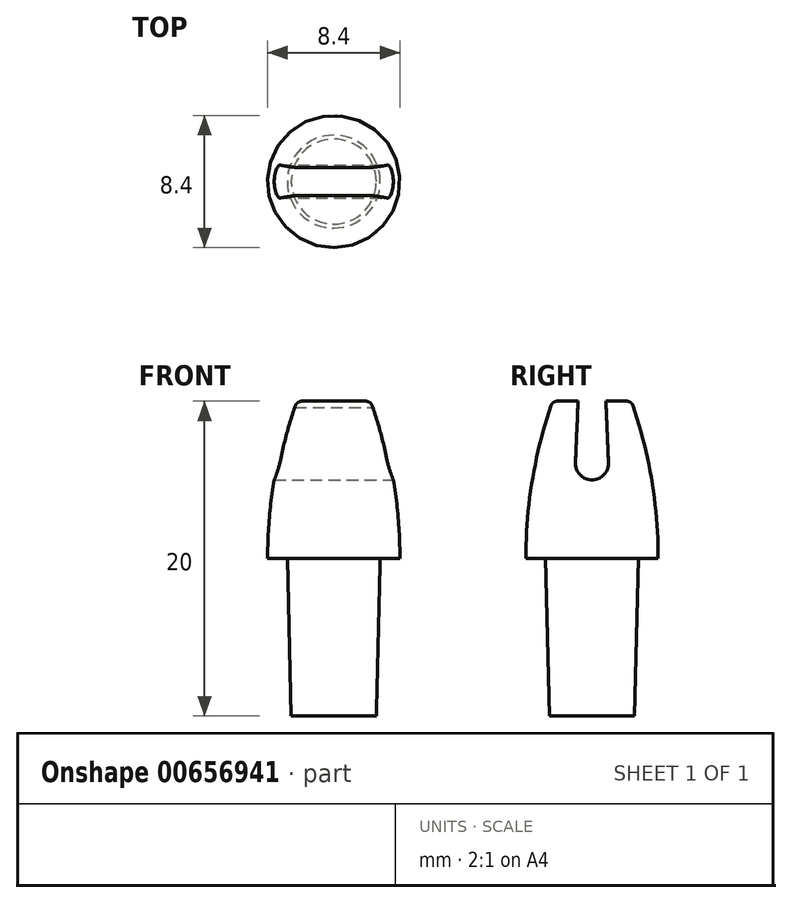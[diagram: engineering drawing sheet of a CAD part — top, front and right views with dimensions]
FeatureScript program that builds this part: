
annotation { "Feature Type Name" : "Feature", "Feature Type Description" : "" }
export const myFeature = defineFeature(function(context is Context, id is Id, definition is map)
    precondition{}
    {
        {
            var Q0;
            Q0=qCreatedBy(makeId("Top.planeOp"),FACE);
            cPlane(context, id + "F0", {"entities" : qUnion([Q0]), "cplaneType" : CPlaneType.OFFSET, "offset" : 10 * mm, "width" : 152.4 * mm, "height" : 152.4 * mm});
        }
        {
            var Q0;
            Q0=qCreatedBy(makeId("Top.planeOp"),FACE);
            var sketch = newSketch(context, id + "F1", { "sketchPlane" : qUnion([Q0])});
            skCircle(sketch, "E0", {"center": v(0, 0) * mm, "radius": 2.7 * mm});
            skSolve(sketch);
        }
        {
            var Q0;
            Q0=qCreatedBy(id+"F0.planeOp",FACE);
            var sketch = newSketch(context, id + "F2", { "sketchPlane" : qUnion([Q0])});
            skCircle(sketch, "E1", {"center": v(0, 0) * mm, "radius": 2.95 * mm});
            skSolve(sketch);
        }
        {
            var Q0;
            Q0=makeQuery(id+"F1.imprint","IMPRINT",FACE,{"disambiguationData":[TD([[makeQuery(id+"F1.imprint","IMPRINT",EDGE,{"derivedFrom":sQuery(id+"F1.wireOp",EDGE,"E0")}),1.0]])]});
            var Q1;
            Q1=makeQuery(id+"F2.imprint","IMPRINT",FACE,{"disambiguationData":[TD([[makeQuery(id+"F2.imprint","IMPRINT",EDGE,{"derivedFrom":sQuery(id+"F2.wireOp",EDGE,"E1")}),1.0]])]});
            loft(context, id + "F3", {"sheetProfilesArray" : [{ "sheetProfileEntities" : qUnion([Q0]) }, { "sheetProfileEntities" : qUnion([Q1]) }]});
        }
        {
            var Q0;
            Q0=qCreatedBy(makeId("Right.planeOp"),FACE);
            var sketch = newSketch(context, id + "F4", { "sketchPlane" : qUnion([Q0])});
            skLineSegment(sketch, "E2", {"start": v(0, 10) * mm, "end": v(-4.2, 10) * mm});
            skArc(sketch, "E3", {"start": v(-4.2, 10) * mm, "mid": v(-3.78, 15.07) * mm, "end": v(-2.5, 20) * mm});
            skLineSegment(sketch, "E4", {"start": v(0, 20) * mm, "end": v(-2.5, 20) * mm});
            skLineSegment(sketch, "E5", {"start": v(0, 10) * mm, "end": v(0, 20) * mm});
            skLineSegment(sketch, "E6", {"start": v(0, 10) * mm, "end": v(0, 0) * mm, "construction": true});
            skSolve(sketch);
        }
        {
            var Q0;
            Q0=makeQuery(id+"F4.imprint","IMPRINT",FACE,{"disambiguationData":[TD([[makeQuery(id+"F4.imprint","IMPRINT",EDGE,{"derivedFrom":sQuery(id+"F4.wireOp",EDGE,"E2")}),-1.0]])]});
            var Q1;
            Q1 = qConstructionFilter(qBodyType(qCreatedBy(id + "F4" ,EDGE), BodyType.WIRE), ConstructionObject.NO);
            var Q2;
            Q2=sQuery(id+"F4.wireOp",EDGE,"E6");
            revolve(context, id + "F5", {"operationType" : NewBodyOperationType.ADD, "entities" : qUnion([Q0]), "surfaceEntities" : qUnion([Q1]), "axis" : qUnion([Q2]), "revolveType" : RevolveType.FULL});
        }
        {
            var Q0;
            Q0=qCreatedBy(makeId("Right.planeOp"),FACE);
            var sketch = newSketch(context, id + "F6", { "sketchPlane" : qUnion([Q0])});
            skLineSegment(sketch, "E7.0", {"start": v(-0.9, 20) * mm, "end": v(0.9, 20) * mm});
            skLineSegment(sketch, "E8", {"start": v(-0.9, 20) * mm, "end": v(-0.9, 19.6) * mm});
            skLineSegment(sketch, "E9", {"start": v(-0.9, 19.6) * mm, "end": v(-1.05, 16.1) * mm});
            skArc(sketch, "E10", {"start": v(-1.05, 16.1) * mm, "mid": v(0, 15) * mm, "end": v(1.05, 16.1) * mm});
            skLineSegment(sketch, "E11.MirrorCS", {"start": v(0.9, 20) * mm, "end": v(0.9, 19.6) * mm});
            skLineSegment(sketch, "E12.MirrorCS", {"start": v(0.9, 19.6) * mm, "end": v(1.05, 16.1) * mm});
            skSolve(sketch);
        }
        {
            var Q0;
            Q0 = qSketchRegion(id + "F6", true);
            extrude(context, id + "F7", {"entities" : qUnion([Q0]), "operationType" : NewBodyOperationType.REMOVE, "endBound" : BoundingType.THROUGH_ALL, "oppositeDirection" : true, "depth" : 25 * mm, "offsetDistance" : 25 * mm, "hasSecondDirection" : true, "secondDirectionBound" : SecondDirectionBoundingType.THROUGH_ALL, "secondDirectionOppositeDirection" : false, "secondDirectionDepth" : 25 * mm});
        }
        {
            var Q0;
            {var subQ0=sQuery(id+"F4.wireOp",EDGE,"E3");var subQ1=sQuery(id+"F4.wireOp",EDGE,"E4");Q0=makeQuery(id+"F7.boolean.opBoolean","SPLIT",EDGE,{"disambiguationData":[TD([makeQuery(id+"F7.opExtrude","SWEPT_FACE",FACE,{"disambiguationData":[OSD([sQuery(id+"F6.wireOp",EDGE,"E8")])]})])],"derivedFrom":makeQuery(id+"F5.opRevolve","SWEPT_EDGE",EDGE,{"disambiguationData":[OSD([subQ0,subQ1])]})});}
            var Q1;
            {var subQ0=sQuery(id+"F4.wireOp",EDGE,"E3");var subQ1=sQuery(id+"F4.wireOp",EDGE,"E4");Q1=makeQuery(id+"F7.boolean.opBoolean","SPLIT",EDGE,{"disambiguationData":[TD([makeQuery(id+"F7.opExtrude","SWEPT_FACE",FACE,{"disambiguationData":[OSD([sQuery(id+"F6.wireOp",EDGE,"E11.MirrorCS")])]})])],"derivedFrom":makeQuery(id+"F5.opRevolve","SWEPT_EDGE",EDGE,{"disambiguationData":[OSD([subQ0,subQ1])]})});}
            fillet(context, id + "F8", {"entities" : qUnion([Q0, Q1]), "radius" : 0.4 * mm, "tangentPropagation" : true, "allowEdgeOverflow" : false});
        }
    });
